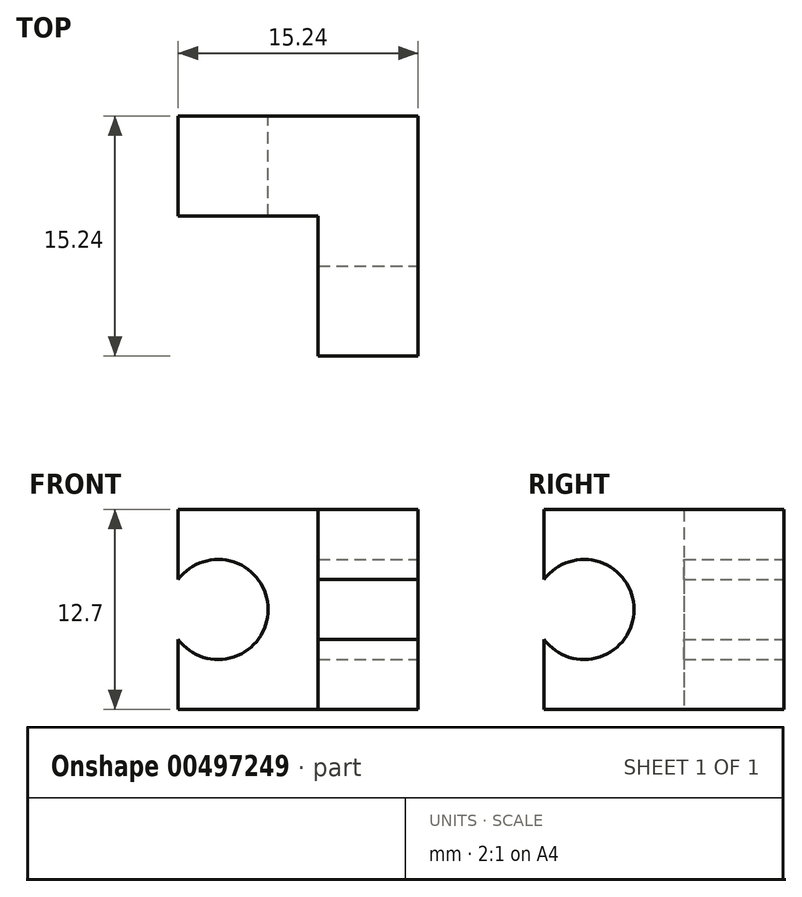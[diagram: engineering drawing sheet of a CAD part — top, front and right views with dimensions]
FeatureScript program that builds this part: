
annotation { "Feature Type Name" : "Feature", "Feature Type Description" : "" }
export const myFeature = defineFeature(function(context is Context, id is Id, definition is map)
    precondition{}
    {
        {
            var Q0;
            Q0=qCreatedBy(makeId("Top.planeOp"),FACE);
            var sketch = newSketch(context, id + "F0", { "sketchPlane" : qUnion([Q0])});
            skLineSegment(sketch, "E0", {"start": v(-3.65, 4.34) * mm, "end": v(5.24, 4.34) * mm});
            skLineSegment(sketch, "E1", {"start": v(5.24, 4.34) * mm, "end": v(5.24, -4.55) * mm});
            skLineSegment(sketch, "E2", {"start": v(5.24, -4.55) * mm, "end": v(11.6, -4.55) * mm});
            skLineSegment(sketch, "E3", {"start": v(11.6, -4.55) * mm, "end": v(11.6, 10.69) * mm});
            skLineSegment(sketch, "E4", {"start": v(11.6, 10.69) * mm, "end": v(-3.65, 10.69) * mm});
            skLineSegment(sketch, "E5", {"start": v(-3.65, 10.69) * mm, "end": v(-3.65, 4.34) * mm});
            skSolve(sketch);
        }
        {
            var Q0;
            Q0 = qSketchRegion(id + "F0", true);
            extrude(context, id + "F1", {"entities" : qUnion([Q0]), "depth" : 12.7 * mm});
        }
        {
            var Q0;
            Q0=makeQuery(id+"F1.opExtrude","SWEPT_FACE",FACE,{"disambiguationData":[OSD([sQuery(id+"F0.wireOp",EDGE,"E4")])]});
            var sketch = newSketch(context, id + "F2", { "sketchPlane" : qUnion([Q0])});
            skPoint(sketch, "E6", {"position": v(1.1, 6.35) * mm});
            skPoint(sketch, "E6.positionSnap0", {"position": v(-11.6, 6.35) * mm});
            skSolve(sketch);
        }
        {
            var Q0;
            Q0=makeQuery(id+"F1.opExtrude","SWEPT_FACE",FACE,{"disambiguationData":[OSD([sQuery(id+"F0.wireOp",EDGE,"E3")])]});
            var sketch = newSketch(context, id + "F3", { "sketchPlane" : qUnion([Q0])});
            skPoint(sketch, "E7", {"position": v(-2.01, 6.35) * mm});
            skPoint(sketch, "E7.positionSnap0", {"position": v(10.69, 6.35) * mm});
            skSolve(sketch);
        }
        {
            var Q0;
            Q0=sQuery(id+"F2.wireOp",VERTEX,"E6");
            var Q1;
            Q1=sQuery(id+"F3.wireOp",VERTEX,"E7");
            var Q2;
            Q2=makeQuery(id+"F1.opExtrude","SWEPT_BODY",BODY,{"disambiguationData":[OSD([sQuery(id+"F0.wireOp",EDGE,"E0"),sQuery(id+"F0.wireOp",EDGE,"E1"),sQuery(id+"F0.wireOp",EDGE,"E2"),sQuery(id+"F0.wireOp",EDGE,"E3"),sQuery(id+"F0.wireOp",EDGE,"E4"),sQuery(id+"F0.wireOp",EDGE,"E5")])]});
            hole(context, id + "F4", {"style" : HoleStyle.SIMPLE, "endStyle" : HoleEndStyle.BLIND, "holeDiameter" : 6.35 * mm, "holeDepth" : 25.4 * mm, "isTappedThrough" : true, "tappedDepth" : 12.7 * mm, "tapClearance" : 3, "startFromSketch" : true, "locations" : qUnion([Q0, Q1]), "scope" : qUnion([Q2])});
        }
    });
